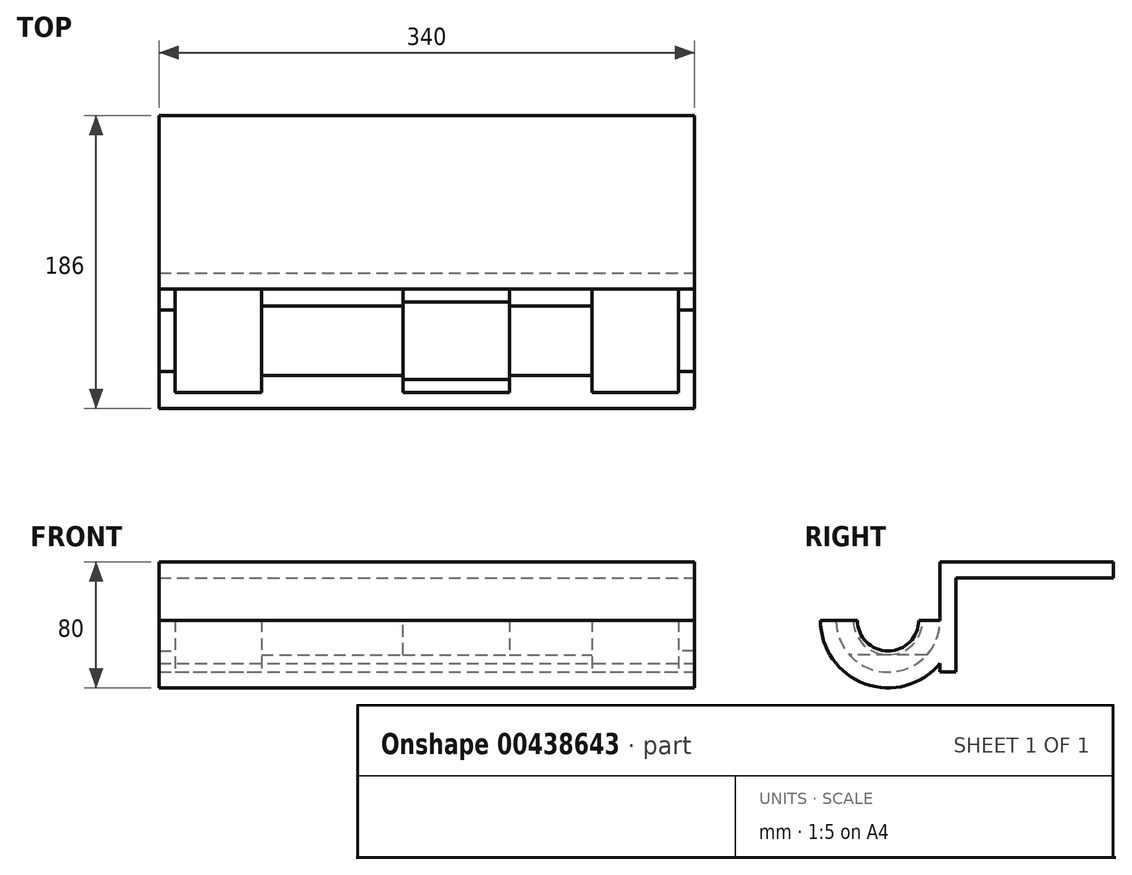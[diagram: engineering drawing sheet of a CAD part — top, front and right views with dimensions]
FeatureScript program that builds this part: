
annotation { "Feature Type Name" : "Feature", "Feature Type Description" : "" }
export const myFeature = defineFeature(function(context is Context, id is Id, definition is map)
    precondition{}
    {
        {
            var Q0;
            Q0=qCreatedBy(makeId("Front.planeOp"),FACE);
            var sketch = newSketch(context, id + "F0", { "sketchPlane" : qUnion([Q0])});
            skLineSegment(sketch, "E0.bottom", {"start": v(-170, 10) * mm, "end": v(170, 10) * mm});
            skLineSegment(sketch, "E0.top", {"start": v(-170, -60) * mm, "end": v(170, -60) * mm});
            skLineSegment(sketch, "E0.left", {"start": v(-170, 10) * mm, "end": v(-170, -60) * mm});
            skLineSegment(sketch, "E0.right", {"start": v(170, 10) * mm, "end": v(170, -60) * mm});
            skSolve(sketch);
        }
        {
            var Q0;
            Q0 = qSketchRegion(id + "F0", true);
            extrude(context, id + "F1", {"entities" : qUnion([Q0]), "depth" : 10 * mm});
        }
        {
            var Q0;
            Q0=qCreatedBy(makeId("Top.planeOp"),FACE);
            var sketch = newSketch(context, id + "F2", { "sketchPlane" : qUnion([Q0])});
            skLineSegment(sketch, "E1.bottom", {"start": v(-170, 0) * mm, "end": v(170, 0) * mm});
            skLineSegment(sketch, "E1.top", {"start": v(-170, 100) * mm, "end": v(170, 100) * mm});
            skLineSegment(sketch, "E1.left", {"start": v(-170, 0) * mm, "end": v(-170, 100) * mm});
            skLineSegment(sketch, "E1.right", {"start": v(170, 0) * mm, "end": v(170, 100) * mm});
            skSolve(sketch);
        }
        {
            var Q0;
            Q0 = qSketchRegion(id + "F2", true);
            extrude(context, id + "F3", {"entities" : qUnion([Q0]), "operationType" : NewBodyOperationType.ADD, "depth" : 10 * mm});
        }
        {
            var Q0;
            Q0=qCreatedBy(makeId("Top.planeOp"),FACE);
            cPlane(context, id + "F4", {"entities" : qUnion([Q0]), "cplaneType" : CPlaneType.OFFSET, "offset" : 27 * mm, "oppositeDirection" : true, "width" : 150 * mm, "height" : 150 * mm});
        }
        {
            var Q0;
            Q0=qCreatedBy(id+"F4.planeOp",FACE);
            var sketch = newSketch(context, id + "F5", { "sketchPlane" : qUnion([Q0])});
            skLineSegment(sketch, "E2", {"start": v(-170, 0) * mm, "end": v(-170, -43) * mm});
            skLineSegment(sketch, "E3", {"start": v(-170, -43) * mm, "end": v(-160, -43) * mm});
            skLineSegment(sketch, "E4", {"start": v(-160, -43) * mm, "end": v(-160, -10) * mm});
            skLineSegment(sketch, "E5", {"start": v(-160, -10) * mm, "end": v(-105, -10) * mm});
            skLineSegment(sketch, "E6", {"start": v(-105, -10) * mm, "end": v(-105, -21) * mm});
            skLineSegment(sketch, "E7", {"start": v(-105, -21) * mm, "end": v(-15, -21) * mm});
            skLineSegment(sketch, "E8", {"start": v(-15, -21) * mm, "end": v(-15, -10) * mm});
            skLineSegment(sketch, "E9", {"start": v(-15, -10) * mm, "end": v(52.5, -10) * mm});
            skLineSegment(sketch, "E10", {"start": v(52.5, -10) * mm, "end": v(52.5, -21) * mm});
            skLineSegment(sketch, "E11", {"start": v(52.5, -21) * mm, "end": v(105, -21) * mm});
            skLineSegment(sketch, "E12", {"start": v(105, -21) * mm, "end": v(105, -10) * mm});
            skLineSegment(sketch, "E13", {"start": v(105, -10) * mm, "end": v(160, -10) * mm});
            skLineSegment(sketch, "E14", {"start": v(160, -10) * mm, "end": v(160, -43) * mm});
            skLineSegment(sketch, "E15", {"start": v(160, -43) * mm, "end": v(170, -43) * mm});
            skLineSegment(sketch, "E16", {"start": v(170, -43) * mm, "end": v(170, 0) * mm});
            skLineSegment(sketch, "E17", {"start": v(170, 0) * mm, "end": v(-170, 0) * mm});
            skSolve(sketch);
        }
        {
            var Q0;
            Q0=qCreatedBy(id+"F4.planeOp",FACE);
            var sketch = newSketch(context, id + "F6", { "sketchPlane" : qUnion([Q0])});
            skLineSegment(sketch, "E18", {"start": v(170, -43) * mm, "end": v(-170, -43) * mm});
            skSolve(sketch);
        }
        {
            var Q0;
            Q0 = qSketchRegion(id + "F5", true);
            var Q1;
            Q1=sQuery(id+"F6.wireOp",EDGE,"E18");
            revolve(context, id + "F7", {"operationType" : NewBodyOperationType.ADD, "entities" : qUnion([Q0]), "axis" : qUnion([Q1]), "revolveType" : RevolveType.ONE_DIRECTION, "angle" : 180 * degree});
        }
        {
            var Q0;
            Q0=qCreatedBy(makeId("Right.planeOp"),FACE);
            var sketch = newSketch(context, id + "F8", { "sketchPlane" : qUnion([Q0])});
            skCircle(sketch, "E19", {"center": v(-43, -27) * mm, "radius": 19.5 * mm});
            skSolve(sketch);
        }
        {
            var Q0;
            Q0=makeQuery(id+"F8.imprint","IMPRINT",FACE,{"disambiguationData":[TD([[makeQuery(id+"F8.imprint","IMPRINT",EDGE,{"derivedFrom":sQuery(id+"F8.wireOp",EDGE,"E19")}),1.0]])]});
            extrude(context, id + "F9", {"entities" : qUnion([Q0]), "operationType" : NewBodyOperationType.REMOVE, "endBound" : BoundingType.THROUGH_ALL, "depth" : 25 * mm});
        }
        {
            var Q0;
            Q0 = qSketchRegion(id + "F8", true);
            extrude(context, id + "F10", {"entities" : qUnion([Q0]), "operationType" : NewBodyOperationType.REMOVE, "endBound" : BoundingType.THROUGH_ALL, "oppositeDirection" : true, "depth" : 25 * mm});
        }
        {
            var Q0;
            Q0=qCreatedBy(id+"F4.planeOp",FACE);
            cPlane(context, id + "F11", {"entities" : qUnion([Q0]), "cplaneType" : CPlaneType.OFFSET, "offset" : 22 * mm, "oppositeDirection" : true, "width" : 150 * mm, "height" : 150 * mm});
        }
        {
            var Q0;
            Q0=qCreatedBy(id+"F11.planeOp",FACE);
            var sketch = newSketch(context, id + "F12", { "sketchPlane" : qUnion([Q0])});
            skLineSegment(sketch, "E20.bottom", {"start": v(-15, -10) * mm, "end": v(52.5, -10) * mm});
            skLineSegment(sketch, "E20.top", {"start": v(-15, -76) * mm, "end": v(52.5, -76) * mm});
            skLineSegment(sketch, "E20.left", {"start": v(-15, -10) * mm, "end": v(-15, -76) * mm});
            skLineSegment(sketch, "E20.right", {"start": v(52.5, -10) * mm, "end": v(52.5, -76) * mm});
            skSolve(sketch);
        }
        {
            var Q0;
            Q0=makeQuery(id+"F12.imprint","IMPRINT",FACE,{"disambiguationData":[TD([[makeQuery(id+"F12.imprint","IMPRINT",EDGE,{"derivedFrom":sQuery(id+"F12.wireOp",EDGE,"E20.bottom")}),-1.0]])]});
            extrude(context, id + "F13", {"entities" : qUnion([Q0]), "operationType" : NewBodyOperationType.ADD, "oppositeDirection" : true, "depth" : 25 * mm});
        }
        {
            var Q0;
            Q0=makeQuery(id+"F13.opExtrude","SWEPT_FACE",FACE,{"disambiguationData":[OSD([sQuery(id+"F12.wireOp",EDGE,"E20.right")])]});
            var sketch = newSketch(context, id + "F14", { "sketchPlane" : qUnion([Q0])});
            skLineSegment(sketch, "E21", {"start": v(-76, -54.57) * mm, "end": v(-76, -74) * mm});
            skLineSegment(sketch, "E22", {"start": v(-76, -74) * mm, "end": v(-10, -74) * mm});
            skLineSegment(sketch, "E23", {"start": v(-10, -74) * mm, "end": v(-10, -54.57) * mm});
            skArc(sketch, "E24", {"start": v(-76, -54.57) * mm, "mid": v(-43, -70) * mm, "end": v(-10, -54.57) * mm});
            skSolve(sketch);
        }
        {
            var Q0;
            Q0 = qSketchRegion(id + "F14", true);
            extrude(context, id + "F15", {"entities" : qUnion([Q0]), "operationType" : NewBodyOperationType.REMOVE, "endBound" : BoundingType.THROUGH_ALL, "oppositeDirection" : true, "depth" : 25 * mm});
        }
    });
